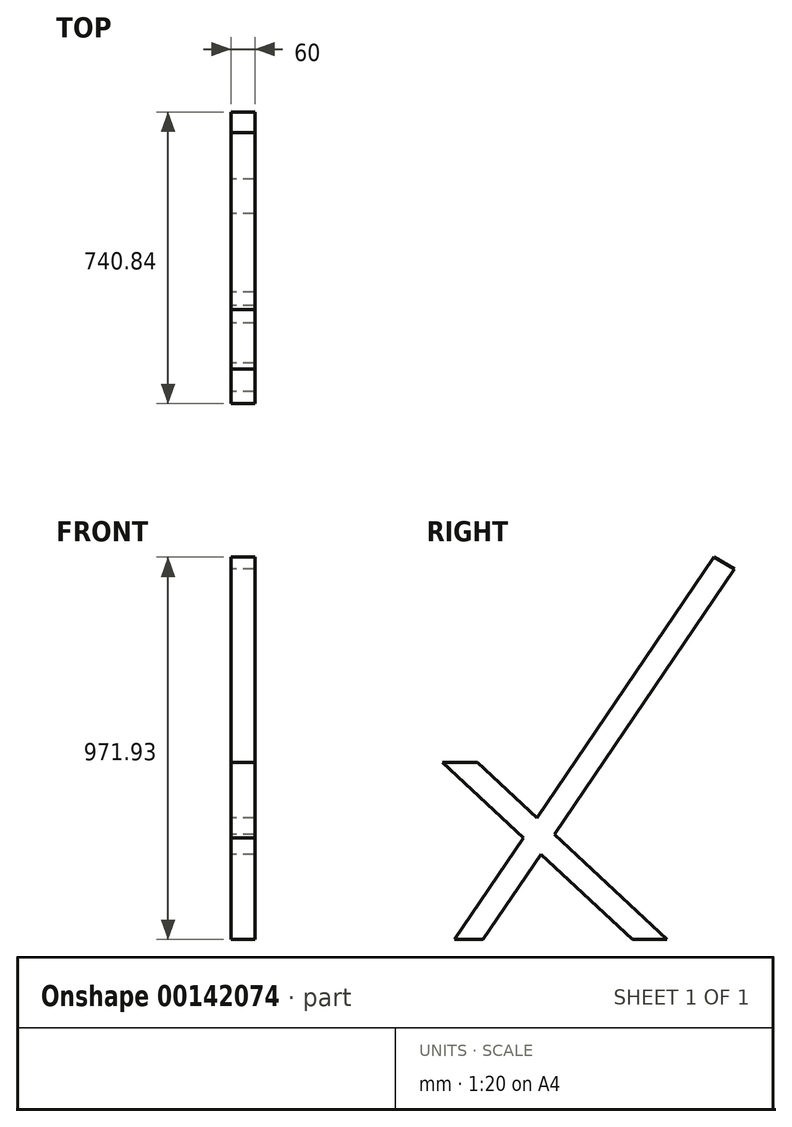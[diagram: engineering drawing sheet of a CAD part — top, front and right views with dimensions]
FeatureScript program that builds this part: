
annotation { "Feature Type Name" : "Feature", "Feature Type Description" : "" }
export const myFeature = defineFeature(function(context is Context, id is Id, definition is map)
    precondition{}
    {
        {
            var Q0;
            Q0=qCreatedBy(makeId("Right.planeOp"),FACE);
            var sketch = newSketch(context, id + "F0", { "sketchPlane" : qUnion([Q0])});
            skLineSegment(sketch, "E0", {"start": v(-170, 0) * mm, "end": v(35.18, -191.53) * mm});
            skLineSegment(sketch, "E1", {"start": v(312.07, -450) * mm, "end": v(400, -450) * mm});
            skLineSegment(sketch, "E2", {"start": v(400, -450) * mm, "end": v(113.65, -182.7) * mm});
            skLineSegment(sketch, "E3", {"start": v(-82.07, 0) * mm, "end": v(-170, 0) * mm});
            skLineSegment(sketch, "E4", {"start": v(-67.52, -450) * mm, "end": v(-140, -450) * mm});
            skLineSegment(sketch, "E5", {"start": v(-140, -450) * mm, "end": v(35.18, -191.53) * mm});
            skLineSegment(sketch, "E6", {"start": v(-67.52, -450) * mm, "end": v(79.58, -232.97) * mm});
            skLineSegment(sketch, "E7", {"start": v(69.26, -141.26) * mm, "end": v(518.75, 521.93) * mm});
            skLineSegment(sketch, "E8", {"start": v(113.65, -182.7) * mm, "end": v(570.84, 491.84) * mm});
            skLineSegment(sketch, "E9", {"start": v(570.84, 491.84) * mm, "end": v(518.75, 521.93) * mm});
            skLineSegment(sketch, "E10", {"start": v(-82.07, 0) * mm, "end": v(165, 0) * mm, "construction": true});
            skLineSegment(sketch, "E11.trimOffspring", {"start": v(69.26, -141.26) * mm, "end": v(-82.07, 0) * mm});
            skLineSegment(sketch, "E12.trimOffspring", {"start": v(79.58, -232.97) * mm, "end": v(312.07, -450) * mm});
            skSolve(sketch);
        }
        {
            var Q0;
            Q0=makeQuery(id+"F0.imprint","IMPRINT",FACE,{"disambiguationData":[TD([[makeQuery(id+"F0.imprint","IMPRINT",EDGE,{"derivedFrom":sQuery(id+"F0.wireOp",EDGE,"E0")}),1.0]])]});
            extrude(context, id + "F1", {"entities" : qUnion([Q0]), "endBound" : BoundingType.SYMMETRIC, "depth" : 60 * mm});
        }
    });
